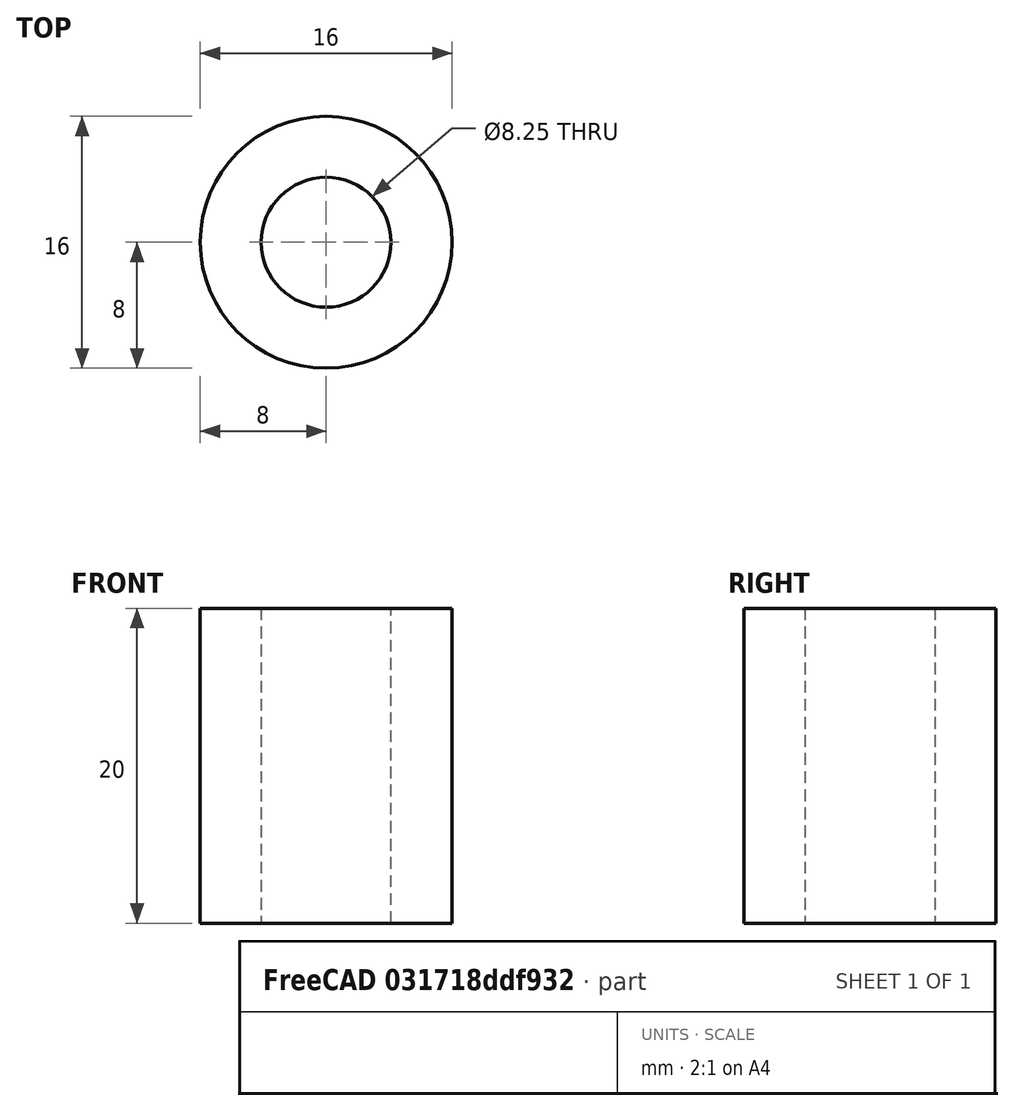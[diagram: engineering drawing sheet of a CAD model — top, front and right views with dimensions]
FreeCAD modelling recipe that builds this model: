
FCSTD DOCUMENT  (FreeCAD 0.18R16146 (Git))
Label: bolt spacer
License: All rights reserved
LicenseURL: http://en.wikipedia.org/wiki/All_rights_reserved
objects: Sketcher::SketchObject×1, PartDesign::Pad×1, PartDesign::Body×1
note: 4 computed .brp shape members not serialized (recipe doc carries the construction recipe); baked Part::Feature solids carry a one-line shape summary decoded from their .brp

FEATURE [Sketcher::SketchObject] Sketch
  MapMode = 5
  Support = -> [XY_Plane]
  sketch-geometry (2):
    g0: Circle CenterX=0 CenterY=0 CenterZ=0 NormalX=0 NormalY=0 NormalZ=1 AngleXU=0 Radius=4.125
    g1: Circle CenterX=0 CenterY=0 CenterZ=0 NormalX=0 NormalY=0 NormalZ=1 AngleXU=0 Radius=8
  constraints (4):
    c: Coincident(g0,g-1)
    c: Coincident(g1,g0)
    c: Diameter(g0) = 8.25
    c: Diameter(g1) = 16
FEATURE [PartDesign::Pad] Pad
  Length = 20
  Length2 = 100
  Profile = -> Sketch
  Type = 0
FEATURE [PartDesign::Body] Body
  Group = -> [Sketch,Pad]
  Origin = -> Origin
  Tip = -> Pad
